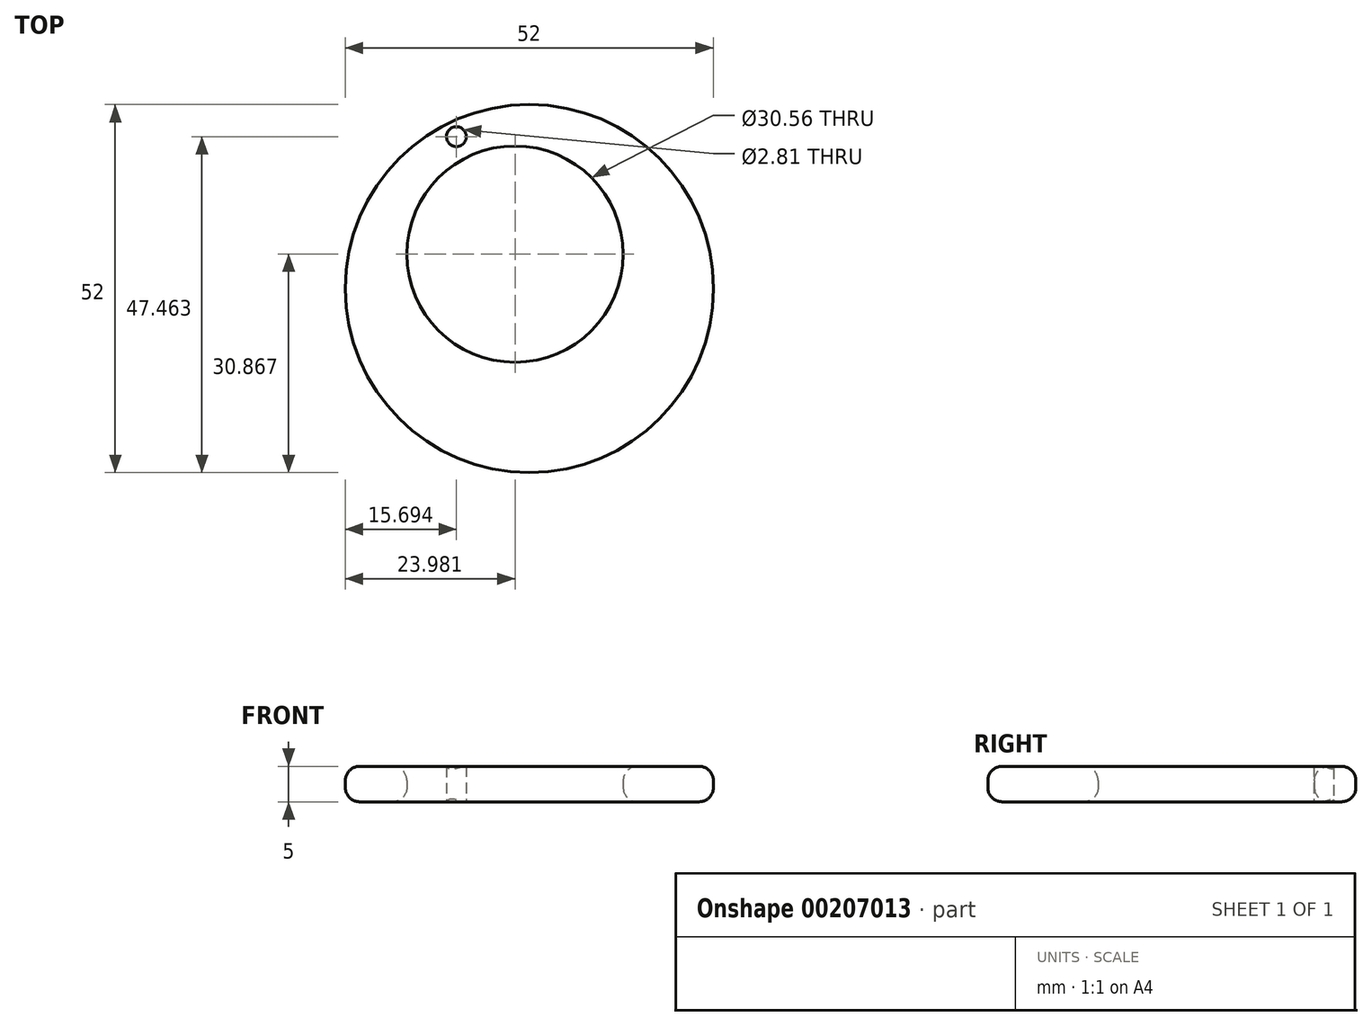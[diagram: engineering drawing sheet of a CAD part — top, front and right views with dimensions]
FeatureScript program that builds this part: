
annotation { "Feature Type Name" : "Feature", "Feature Type Description" : "" }
export const myFeature = defineFeature(function(context is Context, id is Id, definition is map)
    precondition{}
    {
        {
            var Q0;
            Q0=qCreatedBy(makeId("Top.planeOp"),FACE);
            var sketch = newSketch(context, id + "F0", { "sketchPlane" : qUnion([Q0])});
            skCircle(sketch, "E0", {"center": v(-44.87, 39.14) * mm, "radius": 26 * mm});
            skCircle(sketch, "E1", {"center": v(-46.89, 44) * mm, "radius": 15.28 * mm});
            skCircle(sketch, "E2", {"center": v(-55.18, 60.6) * mm, "radius": 1.4 * mm});
            skSolve(sketch);
        }
        {
            var Q0;
            Q0 = qSketchRegion(id + "F0", true);
            extrude(context, id + "F1", {"entities" : qUnion([Q0]), "depth" : 5 * mm});
        }
        {
            var Q0;
            Q0=makeQuery(id+"F1.opExtrude","CAP_EDGE",EDGE,{"disambiguationData":[OSD([sQuery(id+"F0.wireOp",EDGE,"E0")])],"isStart":false});
            var Q1;
            Q1=makeQuery(id+"F1.opExtrude","CAP_EDGE",EDGE,{"disambiguationData":[OSD([sQuery(id+"F0.wireOp",EDGE,"E0")])],"isStart":true});
            var Q2;
            Q2=makeQuery(id+"F1.opExtrude","CAP_EDGE",EDGE,{"disambiguationData":[OSD([sQuery(id+"F0.wireOp",EDGE,"E1")])],"isStart":false});
            var Q3;
            Q3=makeQuery(id+"F1.opExtrude","CAP_EDGE",EDGE,{"disambiguationData":[OSD([sQuery(id+"F0.wireOp",EDGE,"E1")])],"isStart":true});
            fillet(context, id + "F2", {"entities" : qUnion([Q0, Q1, Q2, Q3]), "radius" : 2 * mm, "tangentPropagation" : true, "allowEdgeOverflow" : false});
        }
    });
